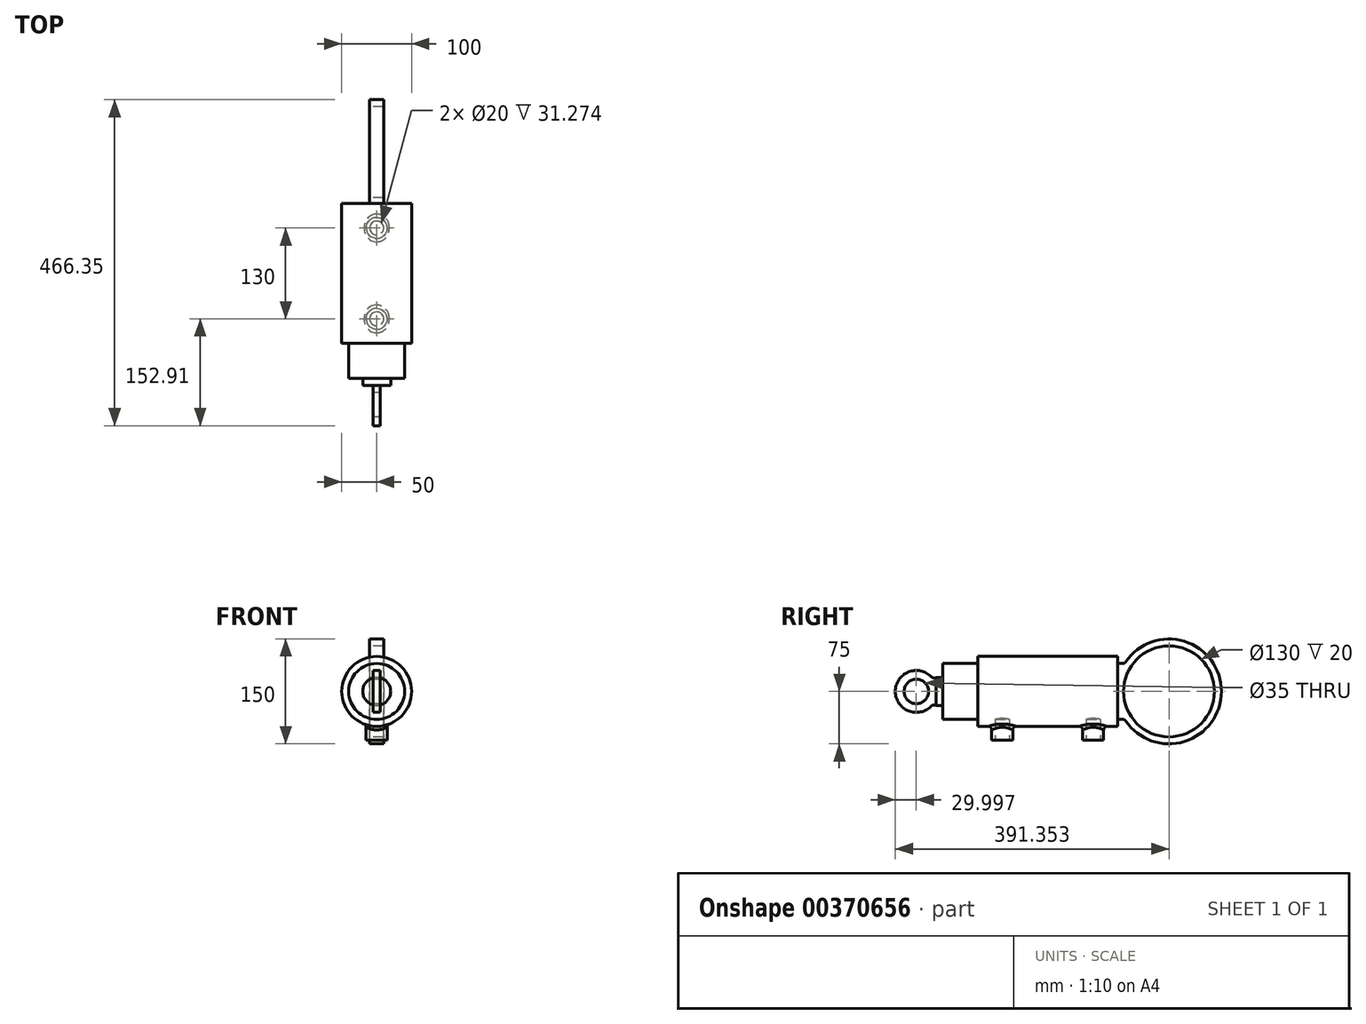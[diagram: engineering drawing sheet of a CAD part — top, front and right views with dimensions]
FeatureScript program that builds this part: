
annotation { "Feature Type Name" : "Feature", "Feature Type Description" : "" }
export const myFeature = defineFeature(function(context is Context, id is Id, definition is map)
    precondition{}
    {
        {
            var Q0;
            Q0=qCreatedBy(makeId("Front.planeOp"),FACE);
            var sketch = newSketch(context, id + "F0", { "sketchPlane" : qUnion([Q0])});
            skCircle(sketch, "E0", {"center": v(0, 0) * mm, "radius": 50 * mm});
            skSolve(sketch);
        }
        {
            var Q0;
            Q0 = qSketchRegion(id + "F0", true);
            extrude(context, id + "F1", {"entities" : qUnion([Q0]), "depth" : 200 * mm});
        }
        {
            var Q0;
            Q0=makeQuery(id+"F1.opExtrude","CAP_FACE",FACE,{"disambiguationData":[OSD([sQuery(id+"F0.wireOp",EDGE,"E0")])],"isStart":false});
            var sketch = newSketch(context, id + "F2", { "sketchPlane" : qUnion([Q0])});
            skCircle(sketch, "E1", {"center": v(0, 0) * mm, "radius": 40 * mm});
            skSolve(sketch);
        }
        {
            var Q0;
            Q0 = qSketchRegion(id + "F2", true);
            extrude(context, id + "F3", {"entities" : qUnion([Q0]), "operationType" : NewBodyOperationType.REMOVE, "oppositeDirection" : true, "depth" : 175 * mm});
        }
        {
            var Q0;
            Q0=qCreatedBy(makeId("Right.planeOp"),FACE);
            var sketch = newSketch(context, id + "F4", { "sketchPlane" : qUnion([Q0])});
            skLineSegment(sketch, "E2", {"start": v(0, 40) * mm, "end": v(10, 40) * mm});
            skLineSegment(sketch, "E3", {"start": v(10, 40) * mm, "end": v(10, -40) * mm});
            skLineSegment(sketch, "E4", {"start": v(10, -40) * mm, "end": v(0, -40) * mm});
            skLineSegment(sketch, "E5", {"start": v(0, -40) * mm, "end": v(0, 0) * mm});
            skLineSegment(sketch, "E6", {"start": v(0, 0) * mm, "end": v(0, 40) * mm});
            skSolve(sketch);
        }
        {
            var Q0;
            Q0 = qSketchRegion(id + "F4", true);
            extrude(context, id + "F5", {"entities" : qUnion([Q0]), "operationType" : NewBodyOperationType.ADD, "depth" : 10 * mm, "hasSecondDirection" : true, "secondDirectionOppositeDirection" : true, "secondDirectionDepth" : 10 * mm});
        }
        {
            var Q0;
            Q0=makeQuery(id+"F5.opExtrude","CAP_FACE",FACE,{"disambiguationData":[OSD([sQuery(id+"F4.wireOp",EDGE,"E2"),sQuery(id+"F4.wireOp",EDGE,"E3"),sQuery(id+"F4.wireOp",EDGE,"E4"),sQuery(id+"F4.wireOp",EDGE,"E5"),sQuery(id+"F4.wireOp",EDGE,"E6")])],"isStart":true});
            var sketch = newSketch(context, id + "F6", { "sketchPlane" : qUnion([Q0])});
            skArc(sketch, "E7", {"start": v(-10, 40) * mm, "mid": v(-148.44, 0) * mm, "end": v(-10, -40) * mm});
            skSolve(sketch);
        }
        {
            var Q0;
            Q0=sQuery(id+"F6.wireOp",EDGE,"E7");
            extrude(context, id + "F7", {"bodyType" : ToolBodyType.SURFACE, "surfaceEntities" : qUnion([Q0]), "oppositeDirection" : true, "depth" : 20 * mm});
        }
        {
            var Q0;
            Q0=makeQuery(id+"F5.opExtrude","CAP_FACE",FACE,{"disambiguationData":[OSD([sQuery(id+"F4.wireOp",EDGE,"E2"),sQuery(id+"F4.wireOp",EDGE,"E3"),sQuery(id+"F4.wireOp",EDGE,"E4"),sQuery(id+"F4.wireOp",EDGE,"E5"),sQuery(id+"F4.wireOp",EDGE,"E6")])],"isStart":true});
            var sketch = newSketch(context, id + "F8", { "sketchPlane" : qUnion([Q0])});
            skLineSegment(sketch, "E8", {"start": v(-10, 40) * mm, "end": v(-10, -40) * mm});
            skArc(sketch, "E9", {"start": v(-10, 40) * mm, "mid": v(-148.44, 0) * mm, "end": v(-10, -40) * mm});
            skSolve(sketch);
        }
        {
            var Q0;
            Q0 = qSketchRegion(id + "F8", true);
            extrude(context, id + "F9", {"entities" : qUnion([Q0]), "operationType" : NewBodyOperationType.ADD, "oppositeDirection" : true, "depth" : 20 * mm});
        }
        {
            var Q0;
            Q0=makeQuery(id+"F9.boolean.opBoolean","MERGE",FACE,{"derivedFrom":[makeQuery(id+"F5.opExtrude","CAP_FACE",FACE,{"disambiguationData":[OSD([sQuery(id+"F4.wireOp",EDGE,"E2"),sQuery(id+"F4.wireOp",EDGE,"E3"),sQuery(id+"F4.wireOp",EDGE,"E4"),sQuery(id+"F4.wireOp",EDGE,"E5"),sQuery(id+"F4.wireOp",EDGE,"E6")])],"isStart":true}),makeQuery(id+"F9.opExtrude","CAP_FACE",FACE,{"disambiguationData":[OSD([sQuery(id+"F8.wireOp",EDGE,"E8"),sQuery(id+"F8.wireOp",EDGE,"E9")])],"isStart":true})]});
            var sketch = newSketch(context, id + "F10", { "sketchPlane" : qUnion([Q0])});
            skCircle(sketch, "E10", {"center": v(-73.44, 0) * mm, "radius": 65 * mm});
            skSolve(sketch);
        }
        {
            var Q0;
            Q0 = qSketchRegion(id + "F10", true);
            extrude(context, id + "F11", {"entities" : qUnion([Q0]), "operationType" : NewBodyOperationType.REMOVE, "oppositeDirection" : true, "depth" : 25 * mm});
        }
        {
            var Q0;
            {var subQ0=sQuery(id+"F4.wireOp",EDGE,"E2");Q0=makeQuery(id+"F9.boolean.opBoolean","MERGE",EDGE,{"derivedFrom":[makeQuery(id+"F5.opExtrude","SWEPT_EDGE",EDGE,{"disambiguationData":[OSD([subQ0,sQuery(id+"F4.wireOp",EDGE,"E3")])]}),makeQuery(id+"F9.opExtrude","SWEPT_EDGE",EDGE,{"disambiguationData":[OSD([subQ0,sQuery(id+"F8.wireOp",EDGE,"E8"),sQuery(id+"F8.wireOp",EDGE,"E9")])]})]});}
            fillet(context, id + "F12", {"entities" : qUnion([Q0]), "radius" : 5 * mm, "tangentPropagation" : true, "allowEdgeOverflow" : false});
        }
        {
            var Q0;
            {var subQ0=sQuery(id+"F4.wireOp",EDGE,"E4");Q0=makeQuery(id+"F9.boolean.opBoolean","MERGE",EDGE,{"derivedFrom":[makeQuery(id+"F5.opExtrude","SWEPT_EDGE",EDGE,{"disambiguationData":[OSD([sQuery(id+"F4.wireOp",EDGE,"E3"),subQ0])]}),makeQuery(id+"F9.opExtrude","SWEPT_EDGE",EDGE,{"disambiguationData":[OSD([subQ0,sQuery(id+"F8.wireOp",EDGE,"E8"),sQuery(id+"F8.wireOp",EDGE,"E9")])]})]});}
            fillet(context, id + "F13", {"entities" : qUnion([Q0]), "radius" : 5 * mm, "tangentPropagation" : true, "allowEdgeOverflow" : false});
        }
        {
            var Q0;
            Q0=qCreatedBy(makeId("Top.planeOp"),FACE);
            cPlane(context, id + "F14", {"entities" : qUnion([Q0]), "cplaneType" : CPlaneType.OFFSET, "offset" : 50 * mm, "oppositeDirection" : true, "width" : 150 * mm, "height" : 150 * mm});
        }
        {
            var Q0;
            Q0=qCreatedBy(id+"F14.planeOp",FACE);
            var sketch = newSketch(context, id + "F15", { "sketchPlane" : qUnion([Q0])});
            skLineSegment(sketch, "E11", {"start": v(0, 0) * mm, "end": v(0, -35) * mm});
            skCircle(sketch, "E12", {"center": v(0, -35) * mm, "radius": 15 * mm});
            skLineSegment(sketch, "E13", {"start": v(0, -35) * mm, "end": v(0, -165) * mm});
            skCircle(sketch, "E14", {"center": v(0, -165) * mm, "radius": 15 * mm});
            skSolve(sketch);
        }
        {
            var Q0;
            Q0=makeQuery(id+"F15.imprint","IMPRINT",FACE,{"disambiguationData":[TD([[makeQuery(id+"F15.imprint","IMPRINT",EDGE,{"derivedFrom":sQuery(id+"F15.wireOp",EDGE,"E14")}),1.0]])]});
            var Q1;
            {var subQ0=sQuery(id+"F15.wireOp",EDGE,"E13");var subQ1=sQuery(id+"F15.wireOp",EDGE,"E11");var subQ2=makeQuery(id+"F15.imprint","INTERSECT",VERTEX,{"derivedFrom":[subQ1,subQ0]});Q1=makeQuery(id+"F15.imprint","IMPRINT",FACE,{"disambiguationData":[TD([[makeQuery(id+"F15.imprint","IMPRINT",EDGE,{"disambiguationData":[TD([[subQ2,1.0]])],"derivedFrom":subQ1}),-1.0]])]});}
            var Q2;
            {var subQ0=sQuery(id+"F15.wireOp",EDGE,"E13");var subQ1=sQuery(id+"F15.wireOp",EDGE,"E11");var subQ2=makeQuery(id+"F15.imprint","INTERSECT",VERTEX,{"derivedFrom":[subQ1,subQ0]});Q2=makeQuery(id+"F15.imprint","IMPRINT",FACE,{"disambiguationData":[TD([[makeQuery(id+"F15.imprint","IMPRINT",EDGE,{"disambiguationData":[TD([[subQ2,1.0]])],"derivedFrom":subQ1}),1.0]])]});}
            extrude(context, id + "F16", {"entities" : qUnion([Q0, Q1, Q2]), "operationType" : NewBodyOperationType.ADD, "oppositeDirection" : true, "depth" : 20 * mm, "hasSecondDirection" : true, "secondDirectionOppositeDirection" : false, "secondDirectionDepth" : 5 * mm});
        }
        {
            var Q0;
            Q0=qCreatedBy(id+"F14.planeOp",FACE);
            cPlane(context, id + "F17", {"entities" : qUnion([Q0]), "cplaneType" : CPlaneType.OFFSET, "offset" : 20 * mm, "oppositeDirection" : true, "width" : 150 * mm, "height" : 150 * mm});
        }
        {
            var Q0;
            Q0=qCreatedBy(id+"F17.planeOp",FACE);
            var sketch = newSketch(context, id + "F18", { "sketchPlane" : qUnion([Q0])});
            skLineSegment(sketch, "E15", {"start": v(0, 0) * mm, "end": v(0, -35) * mm});
            skCircle(sketch, "E16", {"center": v(0, -35) * mm, "radius": 10 * mm});
            skLineSegment(sketch, "E17", {"start": v(0, -35) * mm, "end": v(0, -165) * mm});
            skCircle(sketch, "E18", {"center": v(0, -165) * mm, "radius": 10 * mm});
            skSolve(sketch);
        }
        {
            var Q0;
            Q0 = qSketchRegion(id + "F18", true);
            extrude(context, id + "F19", {"entities" : qUnion([Q0]), "operationType" : NewBodyOperationType.REMOVE, "depth" : 35 * mm});
        }
        {
            var Q0;
            Q0=makeQuery(id+"F16.boolean.opBoolean","INTERSECT",EDGE,{"derivedFrom":[makeQuery(id+"F1.opExtrude","SWEPT_FACE",FACE,{"disambiguationData":[OSD([sQuery(id+"F0.wireOp",EDGE,"E0")])]}),makeQuery(id+"F16.opExtrude","SWEPT_FACE",FACE,{"disambiguationData":[OSD([sQuery(id+"F15.wireOp",EDGE,"E14")])]})]});
            fillet(context, id + "F20", {"entities" : qUnion([Q0]), "radius" : 5 * mm, "tangentPropagation" : true, "allowEdgeOverflow" : false});
        }
        {
            var Q0;
            Q0=makeQuery(id+"F16.boolean.opBoolean","INTERSECT",EDGE,{"derivedFrom":[makeQuery(id+"F1.opExtrude","SWEPT_FACE",FACE,{"disambiguationData":[OSD([sQuery(id+"F0.wireOp",EDGE,"E0")])]}),makeQuery(id+"F16.opExtrude","SWEPT_FACE",FACE,{"disambiguationData":[OSD([sQuery(id+"F15.wireOp",EDGE,"E12")])]})]});
            fillet(context, id + "F21", {"entities" : qUnion([Q0]), "radius" : 5 * mm, "tangentPropagation" : true, "allowEdgeOverflow" : false});
        }
        {
            var Q0;
            Q0=qCreatedBy(makeId("Front.planeOp"),FACE);
            var sketch = newSketch(context, id + "F22", { "sketchPlane" : qUnion([Q0])});
            skCircle(sketch, "E19", {"center": v(0, 0) * mm, "radius": 40 * mm});
            skSolve(sketch);
        }
        {
            var Q0;
            Q0 = qSketchRegion(id + "F22", true);
            extrude(context, id + "F23", {"entities" : qUnion([Q0]), "operationType" : NewBodyOperationType.ADD, "depth" : 250 * mm});
        }
        {
            var Q0;
            Q0=makeQuery(id+"F23.opExtrude","CAP_FACE",FACE,{"disambiguationData":[OSD([sQuery(id+"F22.wireOp",EDGE,"E19")])],"isStart":false});
            var sketch = newSketch(context, id + "F24", { "sketchPlane" : qUnion([Q0])});
            skCircle(sketch, "E20", {"center": v(0, 0) * mm, "radius": 20 * mm});
            skSolve(sketch);
        }
        {
            var Q0;
            Q0 = qSketchRegion(id + "F24", true);
            extrude(context, id + "F25", {"entities" : qUnion([Q0]), "operationType" : NewBodyOperationType.ADD, "depth" : 10 * mm});
        }
        {
            var Q0;
            Q0=makeQuery(id+"F25.opExtrude","CAP_FACE",FACE,{"disambiguationData":[OSD([sQuery(id+"F24.wireOp",EDGE,"E20")])],"isStart":false});
            var sketch = newSketch(context, id + "F26", { "sketchPlane" : qUnion([Q0])});
            skLineSegment(sketch, "E21", {"start": v(5, 19.36) * mm, "end": v(-5, 19.36) * mm});
            skLineSegment(sketch, "E22", {"start": v(-5, -19.36) * mm, "end": v(5, -19.36) * mm});
            skLineSegment(sketch, "E23", {"start": v(-5, 19.36) * mm, "end": v(-5, -19.36) * mm});
            skLineSegment(sketch, "E24", {"start": v(5, 19.36) * mm, "end": v(5, -19.36) * mm});
            skSolve(sketch);
        }
        {
            var Q0;
            Q0 = qSketchRegion(id + "F26", true);
            extrude(context, id + "F27", {"entities" : qUnion([Q0]), "operationType" : NewBodyOperationType.ADD, "depth" : 5 * mm});
        }
        {
            var Q0;
            Q0=makeQuery(id+"F27.opExtrude","SWEPT_FACE",FACE,{"disambiguationData":[OSD([sQuery(id+"F26.wireOp",EDGE,"E23")])]});
            var sketch = newSketch(context, id + "F28", { "sketchPlane" : qUnion([Q0])});
            skArc(sketch, "E25", {"start": v(265, -19.36) * mm, "mid": v(317.91, 0) * mm, "end": v(265, 19.36) * mm});
            skSolve(sketch);
        }
        {
            var Q0;
            Q0=makeQuery(id+"F28.imprint","IMPRINT",FACE,{"disambiguationData":[TD([[makeQuery(id+"F28.imprint","IMPRINT",EDGE,{"derivedFrom":sQuery(id+"F28.wireOp",EDGE,"E25")}),1.0]])]});
            extrude(context, id + "F29", {"entities" : qUnion([Q0]), "operationType" : NewBodyOperationType.ADD, "oppositeDirection" : true, "depth" : 10 * mm});
        }
        {
            var Q0;
            {var subQ0=sQuery(id+"F26.wireOp",EDGE,"E21");Q0=makeQuery(id+"F29.boolean.opBoolean","MERGE",EDGE,{"derivedFrom":[makeQuery(id+"F27.opExtrude","CAP_EDGE",EDGE,{"disambiguationData":[OSD([subQ0])],"isStart":false}),makeQuery(id+"F29.opExtrude","SWEPT_EDGE",EDGE,{"disambiguationData":[OSD([sQuery(id+"F24.wireOp",EDGE,"E20"),subQ0,sQuery(id+"F26.wireOp",EDGE,"E23"),sQuery(id+"F28.wireOp",EDGE,"E25")])]})]});}
            fillet(context, id + "F30", {"entities" : qUnion([Q0]), "radius" : 5 * mm, "tangentPropagation" : true, "allowEdgeOverflow" : false});
        }
        {
            var Q0;
            {var subQ0=sQuery(id+"F26.wireOp",EDGE,"E22");Q0=makeQuery(id+"F29.boolean.opBoolean","MERGE",EDGE,{"derivedFrom":[makeQuery(id+"F27.opExtrude","CAP_EDGE",EDGE,{"disambiguationData":[OSD([subQ0])],"isStart":false}),makeQuery(id+"F29.opExtrude","SWEPT_EDGE",EDGE,{"disambiguationData":[OSD([sQuery(id+"F24.wireOp",EDGE,"E20"),subQ0,sQuery(id+"F26.wireOp",EDGE,"E23"),sQuery(id+"F28.wireOp",EDGE,"E25")])]})]});}
            fillet(context, id + "F31", {"entities" : qUnion([Q0]), "radius" : 5 * mm, "tangentPropagation" : true, "allowEdgeOverflow" : false});
        }
        {
            var Q0;
            {var subQ0=sQuery(id+"F26.wireOp",EDGE,"E23");Q0=makeQuery(id+"F29.boolean.opBoolean","MERGE",FACE,{"derivedFrom":[makeQuery(id+"F27.opExtrude","SWEPT_FACE",FACE,{"disambiguationData":[OSD([subQ0])]}),makeQuery(id+"F29.opExtrude","CAP_FACE",FACE,{"disambiguationData":[OSD([subQ0,sQuery(id+"F28.wireOp",EDGE,"E25")])],"isStart":true})]});}
            var sketch = newSketch(context, id + "F32", { "sketchPlane" : qUnion([Q0])});
            skCircle(sketch, "E26", {"center": v(287.91, 0) * mm, "radius": 17.5 * mm});
            skSolve(sketch);
        }
        {
            var Q0;
            Q0=makeQuery(id+"F32.imprint","IMPRINT",FACE,{"disambiguationData":[TD([[makeQuery(id+"F32.imprint","IMPRINT",EDGE,{"derivedFrom":sQuery(id+"F32.wireOp",EDGE,"E26")}),1.0]])]});
            var Q1;
            Q1=sQuery(id+"F32.wireOp",EDGE,"E26");
            extrude(context, id + "F33", {"entities" : qUnion([Q0]), "operationType" : NewBodyOperationType.REMOVE, "surfaceEntities" : qUnion([Q1]), "oppositeDirection" : true, "depth" : 25 * mm});
        }
    });
